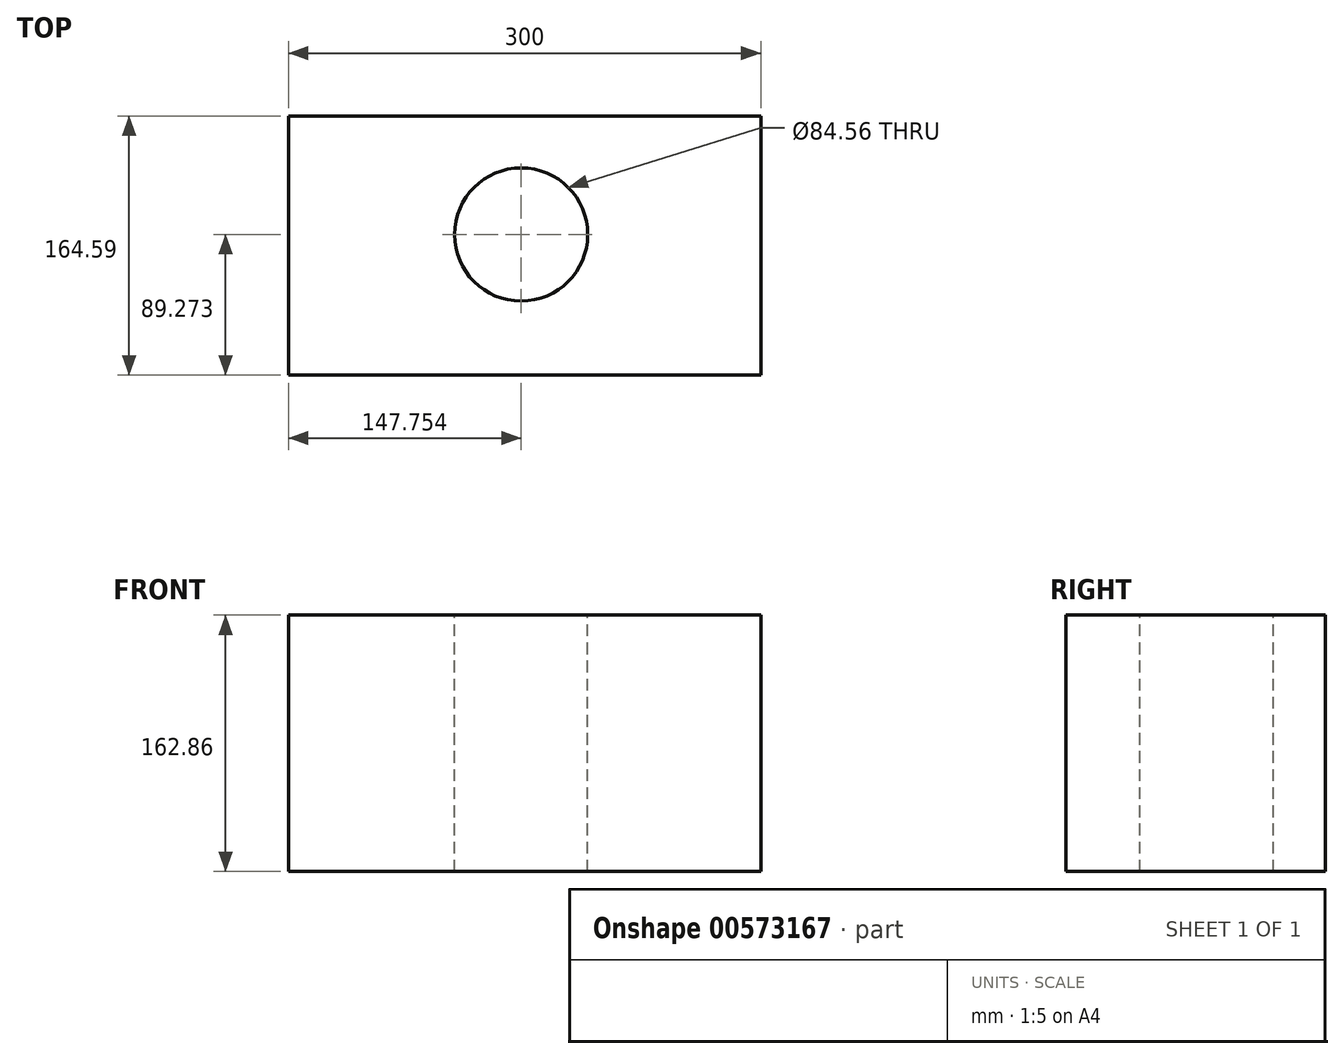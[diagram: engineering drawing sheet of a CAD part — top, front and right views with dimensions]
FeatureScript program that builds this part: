
annotation { "Feature Type Name" : "Feature", "Feature Type Description" : "" }
export const myFeature = defineFeature(function(context is Context, id is Id, definition is map)
    precondition{}
    {
        {
            var Q0;
            Q0=qCreatedBy(makeId("Front.planeOp"),FACE);
            var sketch = newSketch(context, id + "F0", { "sketchPlane" : qUnion([Q0])});
            skLineSegment(sketch, "E0.bottom", {"start": v(0, 0) * mm, "end": v(300, 0) * mm});
            skLineSegment(sketch, "E0.top", {"start": v(0, 162.86) * mm, "end": v(300, 162.86) * mm});
            skLineSegment(sketch, "E0.left", {"start": v(0, 0) * mm, "end": v(0, 162.86) * mm});
            skLineSegment(sketch, "E0.right", {"start": v(300, 0) * mm, "end": v(300, 162.86) * mm});
            skSolve(sketch);
        }
        {
            var Q0;
            Q0 = qSketchRegion(id + "F0", true);
            extrude(context, id + "F1", {"entities" : qUnion([Q0]), "depth" : 164.6 * mm, "offsetDistance" : 25.4 * mm});
        }
        {
            var Q0;
            Q0=makeQuery(id+"F1.opExtrude","SWEPT_FACE",FACE,{"disambiguationData":[OSD([sQuery(id+"F0.wireOp",EDGE,"E0.top")])]});
            var sketch = newSketch(context, id + "F2", { "sketchPlane" : qUnion([Q0])});
            skCircle(sketch, "E1", {"center": v(147.75, -75.32) * mm, "radius": 42.28 * mm});
            skSolve(sketch);
        }
        {
            var Q0;
            Q0=makeQuery(id+"F2.imprint","IMPRINT",FACE,{"disambiguationData":[TD([[makeQuery(id+"F2.imprint","IMPRINT",EDGE,{"derivedFrom":sQuery(id+"F2.wireOp",EDGE,"E1")}),1.0]])]});
            extrude(context, id + "F3", {"entities" : qUnion([Q0]), "operationType" : NewBodyOperationType.REMOVE, "oppositeDirection" : true, "depth" : 337.82 * mm, "offsetDistance" : 25.4 * mm});
        }
    });
